# Revit family: NLRS_63_LF_LUM-DL02AC-DCEM_luminaid
name_source: partatom
category: Lighting Fixtures
revit_build: Autodesk Revit 2018 (Build: 20190510_1515(x64)
units: mm (PartAtom-declared; Revit-internal decimal feet)

## family parameters
Always vertical = Yes
Cut with Voids When Loaded = No
Light Source = Yes
Part Type = Normal
Room Calculation Point = No
Round Connector Dimension = Use Diameter
Shared = No
Work Plane-Based = No

## types (3) — shared parameters
Ambient temp range = +5°C~+50°C
Angle = 180.00°
Autonomy = 2 hr
Color Filter = 16777215
Depth = 130 mm  [stored 0.426509 ft]
Dimming Lamp Color Temperature Shift = <None>
Emit from Line Length = 180 mm  [stored 0.590551 ft]
Housing- IP = IP65
Input Voltage & frequency = 200-250, 50 Hz
Length = 180 mm  [stored 0.590551 ft]
Lumen = 5590 lm
Manufacturer = LUMINAID B.V.
Power = 14 W
Product Brand = DATALUX.AC
Tilt Angle = 90.00°
Upside = No
Weight = 0.88 kg

## per-type parameters (varying)
| type | Height | Lens type | Photometric Web File |
| LUM-DL02AC-DCEM-06NB | 100 mm  [stored 0.328084 ft] | Narrow beam | LUM-DL02AC-DCEM-06NB.ies |
| LUM-DL02AC-DCEM-06WB | 101 mm | Wide beam | LUM-DL02AC-DCEM-06WB.ies |
| LUM-DL02AC-DCEM-06UW | 102 mm | Ultrawide beam | LUM-DL02AC-DCEM-06UW.ies |

note: column(s) folded — value = type name in every type: Article code

note: [stored X ft] marks values corroborated as IEEE doubles in the binary element streams (Revit-internal decimal feet)

## geometry (parser evidence)
native form markers: Sweep x9
no freeform markers — native parametric forms only
